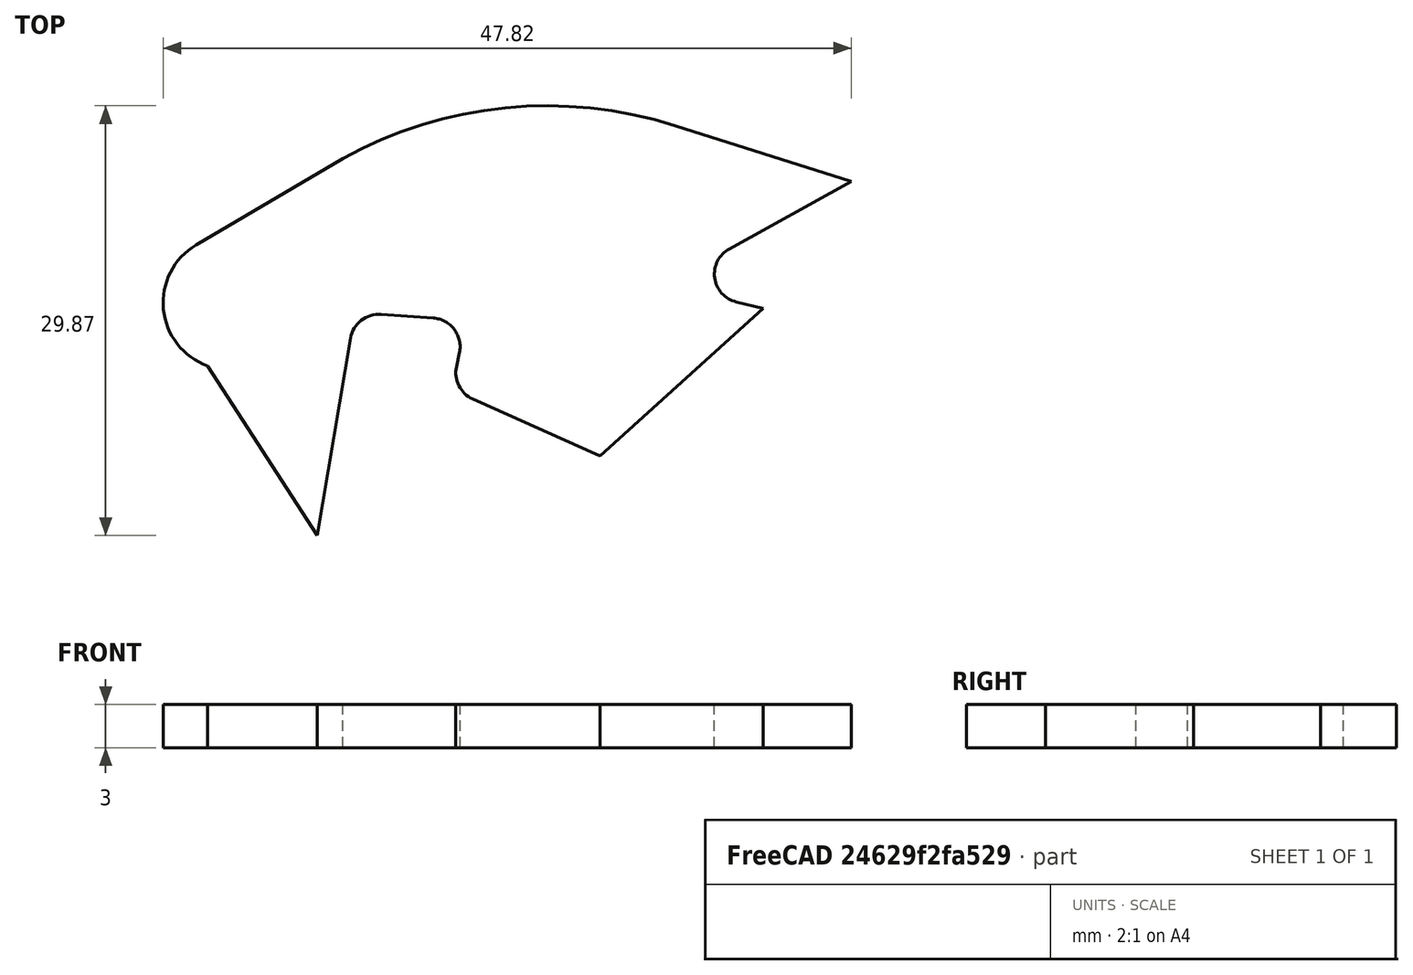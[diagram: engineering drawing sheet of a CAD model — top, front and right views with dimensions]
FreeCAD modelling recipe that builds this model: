
FCSTD DOCUMENT  (FreeCAD 0.17R13523 (Git))
Label: irregular
License: All rights reserved
LicenseURL: http://en.wikipedia.org/wiki/All_rights_reserved
objects: Sketcher::SketchObject×1, PartDesign::Pad×1, PartDesign::Fillet×1, PartDesign::Body×1
note: 5 computed .brp shape members not serialized (recipe doc carries the construction recipe); baked Part::Feature solids carry a one-line shape summary decoded from their .brp

FEATURE [Sketcher::SketchObject] Sketch
  MapMode = 5
  Support = -> [XY_Plane]
  sketch-geometry (12):
    g0: LineSegment StartX=-15.5601 StartY=12.9753 StartZ=0 EndX=-25.7398 EndY=6.96302 EndZ=0
    g1: ArcOfCircle CenterX=-23.3683 CenterY=2.94785 CenterZ=0 NormalX=0 NormalY=0 NormalZ=1 AngleXU=0 Radius=4.66319 StartAngle=2.10429 EndAngle=4.37042
    g2: LineSegment StartX=-24.9321 StartY=-1.44532 StartZ=0 EndX=-17.3205 EndY=-13.2291 EndZ=0
    g3: LineSegment StartX=-17.3205 StartY=-13.2291 StartZ=0 EndX=-14.702 EndY=2.26394 EndZ=0
    g4: LineSegment StartX=-14.702 StartY=2.26394 StartZ=0 EndX=-6.95548 EndY=1.71841 EndZ=0
    g5: LineSegment StartX=-6.95548 StartY=1.71841 StartZ=0 EndX=-7.99198 EndY=-3.08223 EndZ=0
    g6: LineSegment StartX=-7.99198 StartY=-3.08223 StartZ=0 EndX=2.3185 EndY=-7.71922 EndZ=0
    g7: LineSegment StartX=2.3185 StartY=-7.71922 StartZ=0 EndX=13.6655 EndY=2.5367 EndZ=0
    g8: LineSegment StartX=13.6655 StartY=2.5367 StartZ=0 EndX=6.84637 EndY=4.22784 EndZ=0
    g9: LineSegment StartX=6.84637 StartY=4.22784 StartZ=0 EndX=19.792 EndY=11.3707 EndZ=0
    g10: LineSegment StartX=19.792 StartY=11.3707 StartZ=0 EndX=7.52089 EndY=15.2629 EndZ=0
    g11: ArcOfCircle CenterX=-1.35842 CenterY=-12.7315 CenterZ=0 NormalX=0 NormalY=0 NormalZ=1 AngleXU=0 Radius=29.3688 StartAngle=1.26365 EndAngle=2.07552
  constraints (12):
    c: Tangent(g0,g1) = -1.5708
    c: Coincident(g1,g2)
    c: Coincident(g2,g3)
    c: Coincident(g3,g4)
    c: Coincident(g4,g5)
    c: Coincident(g5,g6)
    c: Coincident(g6,g7)
    c: Coincident(g7,g8)
    c: Coincident(g8,g9)
    c: Coincident(g9,g10)
    c: Tangent(g10,g11) = -1.5708
    c: Coincident(g11,g0)
FEATURE [PartDesign::Pad] Pad
  Length = 3
  Length2 = 100
  Profile = -> Sketch
  Type = 0
FEATURE [PartDesign::Fillet] Fillet
  Base = -> Pad [Edge11,Edge14,Edge17,Edge26]
  BaseFeature = -> Pad
  Radius = 2
FEATURE [PartDesign::Body] Body
  Group = -> [Sketch,Pad,Fillet]
  Origin = -> Origin
  Tip = -> Fillet
